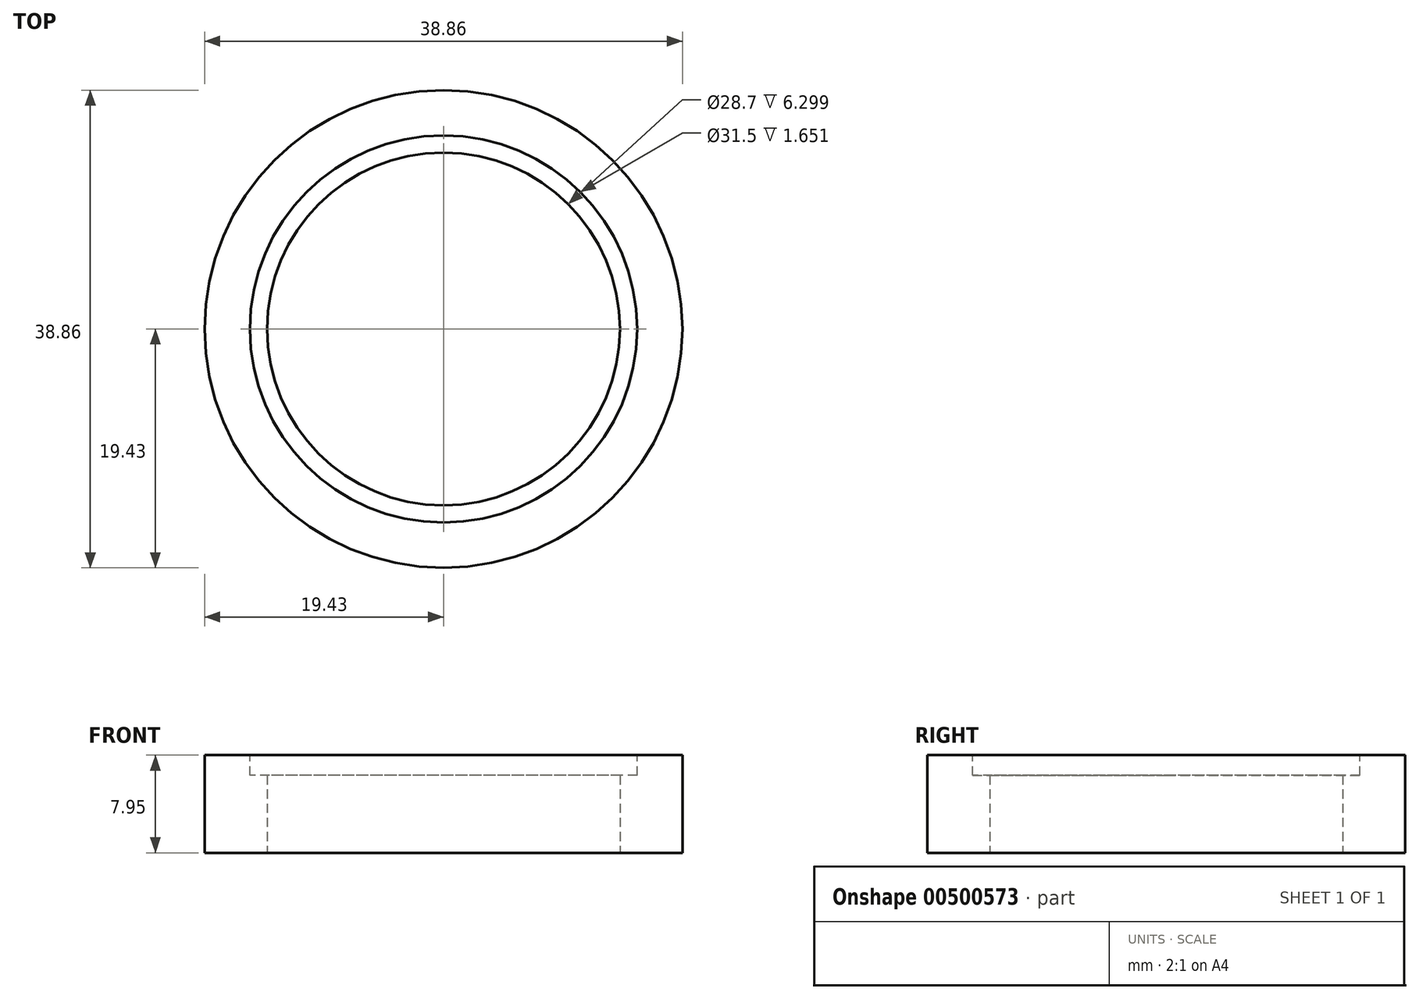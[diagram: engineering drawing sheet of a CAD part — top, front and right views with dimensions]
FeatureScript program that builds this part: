
annotation { "Feature Type Name" : "Feature", "Feature Type Description" : "" }
export const myFeature = defineFeature(function(context is Context, id is Id, definition is map)
    precondition{}
    {
        {
            var Q0;
            Q0=qCreatedBy(makeId("Top.planeOp"),FACE);
            var sketch = newSketch(context, id + "F0", { "sketchPlane" : qUnion([Q0])});
            skCircle(sketch, "E0", {"center": v(0, 0) * mm, "radius": 14.35 * mm});
            skCircle(sketch, "E1.0", {"center": v(0, 0) * mm, "radius": 19.43 * mm});
            skSolve(sketch);
        }
        {
            var Q0;
            Q0=makeQuery(id+"F0.imprint","IMPRINT",FACE,{"disambiguationData":[TD([[makeQuery(id+"F0.imprint","IMPRINT",EDGE,{"derivedFrom":sQuery(id+"F0.wireOp",EDGE,"E0")}),-1.0]])]});
            extrude(context, id + "F1", {"entities" : qUnion([Q0]), "depth" : 7.95 * mm, "offsetDistance" : 25.4 * mm});
        }
        {
            var Q0;
            Q0=makeQuery(id+"F1.opExtrude","CAP_FACE",FACE,{"disambiguationData":[OSD([sQuery(id+"F0.wireOp",EDGE,"E0"),sQuery(id+"F0.wireOp",EDGE,"E1.0")])],"isStart":false});
            var sketch = newSketch(context, id + "F2", { "sketchPlane" : qUnion([Q0])});
            skCircle(sketch, "E2.0", {"center": v(0, 0) * mm, "radius": 15.75 * mm});
            skSolve(sketch);
        }
        {
            var Q0;
            Q0=makeQuery(id+"F2.imprint","IMPRINT",FACE,{"disambiguationData":[TD([[makeQuery(id+"F2.imprint","IMPRINT",EDGE,{"derivedFrom":sQuery(id+"F2.wireOp",EDGE,"E2.0")}),1.0]])]});
            var Q1;
            Q1=sQuery(id+"F2.wireOp",EDGE,"E2.0");
            extrude(context, id + "F3", {"entities" : qUnion([Q0]), "operationType" : NewBodyOperationType.REMOVE, "surfaceEntities" : qUnion([Q1]), "oppositeDirection" : true, "depth" : 1.65 * mm, "offsetDistance" : 25.4 * mm});
        }
    });
